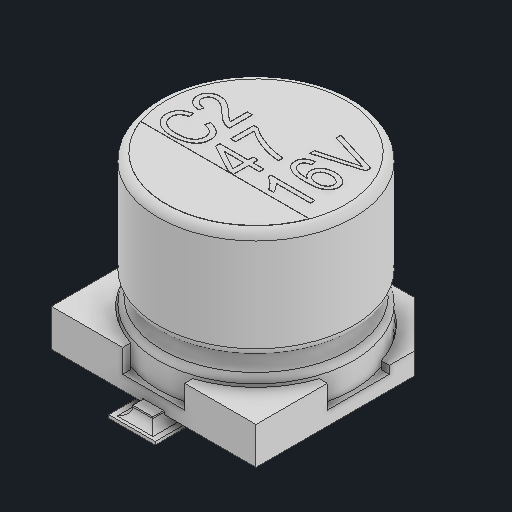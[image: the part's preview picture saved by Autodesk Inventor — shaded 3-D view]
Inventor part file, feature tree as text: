
AUTODESK INVENTOR PART (.ipt)
format: ipt  version: 2023 (Build 270158000, 158)  size: 371,712 bytes
history: native  units: in
note: dims shown in document units (in); Inventor stores cm internally (conversion verified against a paired STEP export)
features: fillet x1, other x1
ambient origin geometry x8: Origin, YZ Plane, XZ Plane, XY Plane, X Axis, Y Axis, Z Axis, Center Point
bodies: Solid1 (feature_tree), Solid2 (feature_tree)
feature tree (2):
  fillet  "Fillet1"  [1 undecoded]
  other  "Boss-Extrude7"
note: 1 required parameter value undecoded (feature->parameter linkage not recoverable at this tier; creation-order binding heuristic only, values carry confidence <= 0.55)
